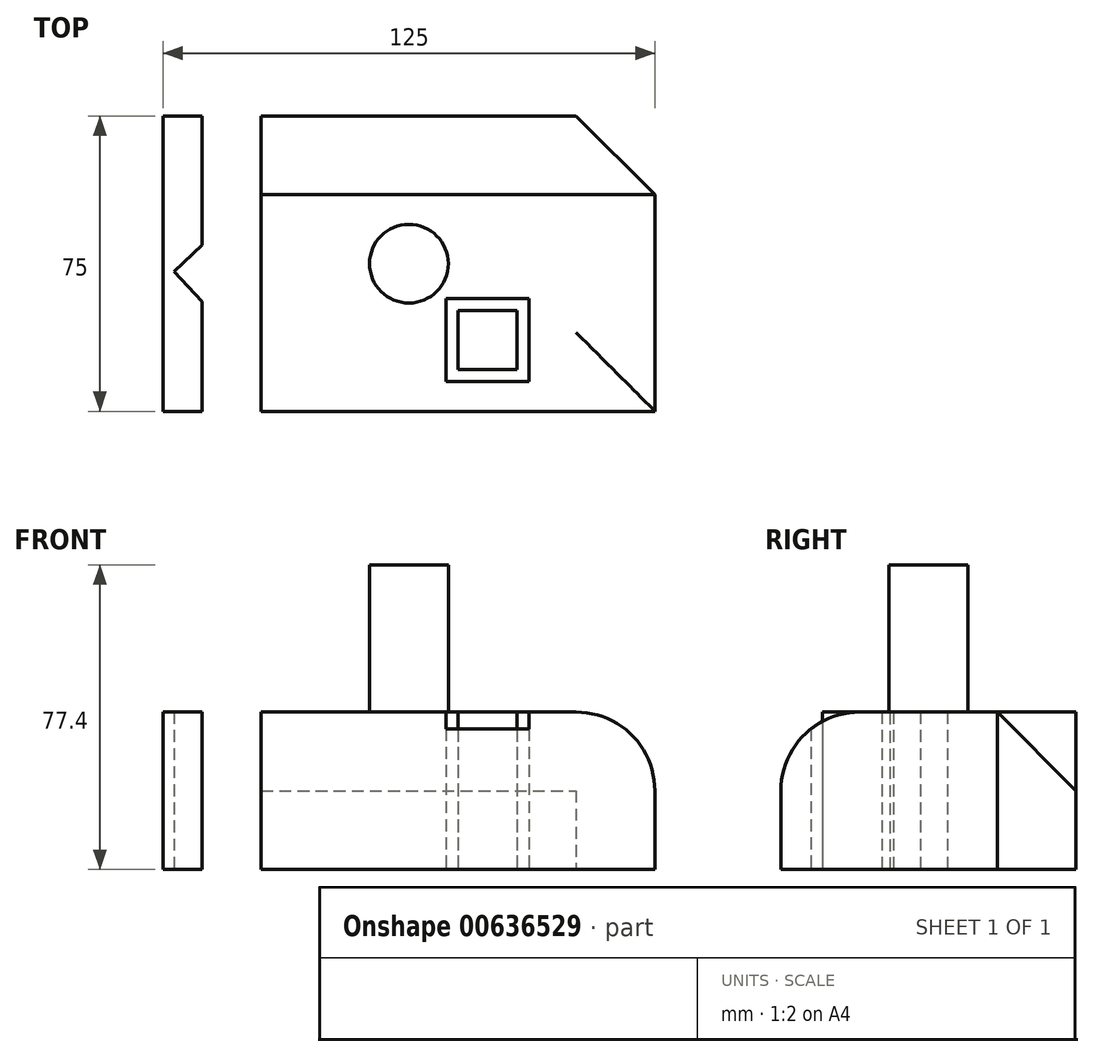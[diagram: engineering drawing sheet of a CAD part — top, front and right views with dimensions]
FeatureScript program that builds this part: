
annotation { "Feature Type Name" : "Feature", "Feature Type Description" : "" }
export const myFeature = defineFeature(function(context is Context, id is Id, definition is map)
    precondition{}
    {
        {
            var Q0;
            Q0=qCreatedBy(makeId("Top.planeOp"),FACE);
            var sketch = newSketch(context, id + "F0", { "sketchPlane" : qUnion([Q0])});
            skLineSegment(sketch, "E0.bottom", {"start": v(62.5, 37.5) * mm, "end": v(-62.5, 37.5) * mm});
            skLineSegment(sketch, "E0.top", {"start": v(62.5, -37.5) * mm, "end": v(-62.5, -37.5) * mm});
            skLineSegment(sketch, "E0.left", {"start": v(62.5, 37.5) * mm, "end": v(62.5, -37.5) * mm});
            skLineSegment(sketch, "E0.right", {"start": v(-62.5, 37.5) * mm, "end": v(-62.5, -37.5) * mm});
            skPoint(sketch, "E0.middle", {"position": v(0, 0) * mm});
            skLineSegment(sketch, "E1.bottom", {"start": v(-52.5, 37.5) * mm, "end": v(-37.5, 37.5) * mm});
            skLineSegment(sketch, "E1.top", {"start": v(-52.5, -37.5) * mm, "end": v(-37.5, -37.5) * mm});
            skLineSegment(sketch, "E1.left", {"start": v(-52.5, 37.5) * mm, "end": v(-52.5, -37.5) * mm});
            skLineSegment(sketch, "E1.right", {"start": v(-37.5, 37.5) * mm, "end": v(-37.5, -37.5) * mm});
            skCircle(sketch, "E2", {"center": v(0, 0) * mm, "radius": 10 * mm});
            skSolve(sketch);
        }
        {
            var Q0;
            {var subQ0=sQuery(id+"F0.wireOp",EDGE,"E0.right");Q0=makeQuery(id+"F0.imprint","IMPRINT",FACE,{"disambiguationData":[TD([[makeQuery(id+"F0.imprint","IMPRINT",EDGE,{"derivedFrom":subQ0}),1.0]])]});}
            var Q1;
            Q1=makeQuery(id+"F0.imprint","IMPRINT",FACE,{"disambiguationData":[TD([[makeQuery(id+"F0.imprint","IMPRINT",EDGE,{"derivedFrom":sQuery(id+"F0.wireOp",EDGE,"E1.bottom")}),-1.0]])]});
            var Q2;
            {var subQ1=sQuery(id+"F0.wireOp",EDGE,"E0.left");Q2=makeQuery(id+"F0.imprint","IMPRINT",FACE,{"disambiguationData":[TD([[makeQuery(id+"F0.imprint","IMPRINT",EDGE,{"derivedFrom":subQ1}),-1.0]])]});}
            var Q3;
            Q3=makeQuery(id+"F0.imprint","IMPRINT",FACE,{"disambiguationData":[TD([[makeQuery(id+"F0.imprint","IMPRINT",EDGE,{"derivedFrom":sQuery(id+"F0.wireOp",EDGE,"E2")}),1.0]])]});
            extrude(context, id + "F1", {"entities" : qUnion([Q0, Q1, Q2, Q3]), "depth" : 40 * mm, "offsetDistance" : 25 * mm});
        }
        {
            var Q0;
            Q0=makeQuery(id+"F1.opExtrude","CAP_FACE",FACE,{"disambiguationData":[OSD([sQuery(id+"F0.wireOp",EDGE,"E0.bottom"),sQuery(id+"F0.wireOp",EDGE,"E0.top"),sQuery(id+"F0.wireOp",EDGE,"E0.left"),sQuery(id+"F0.wireOp",EDGE,"E0.right"),sQuery(id+"F0.wireOp",EDGE,"E1.bottom"),sQuery(id+"F0.wireOp",EDGE,"E1.top")])],"isStart":true});
            var sketch = newSketch(context, id + "F2", { "sketchPlane" : qUnion([Q0])});
            skCircle(sketch, "E3", {"center": v(0, 0) * mm, "radius": 10 * mm});
            skLineSegment(sketch, "E4", {"start": v(-59.7, 2) * mm, "end": v(-43, 19.7) * mm});
            skLineSegment(sketch, "E5", {"start": v(-43, 19.7) * mm, "end": v(-25.3, 3) * mm});
            skLineSegment(sketch, "E6", {"start": v(-25.3, 3) * mm, "end": v(-42, -14.7) * mm});
            skLineSegment(sketch, "E7", {"start": v(-42, -14.7) * mm, "end": v(-59.7, 2) * mm});
            skLineSegment(sketch, "E8", {"start": v(-59.7, 2) * mm, "end": v(-25.3, 3) * mm, "construction": true});
            skLineSegment(sketch, "E9", {"start": v(-43, 19.7) * mm, "end": v(-42, -14.7) * mm, "construction": true});
            skPoint(sketch, "E10", {"position": v(-42.5, 2.5) * mm});
            skArc(sketch, "E11", {"start": v(33.7, -37.5) * mm, "mid": v(50.04, 0.25) * mm, "end": v(32.6, 37.5) * mm});
            skLineSegment(sketch, "E12.bottom", {"start": v(27.45, 11.88) * mm, "end": v(12.45, 11.88) * mm});
            skLineSegment(sketch, "E12.top", {"start": v(27.45, 26.88) * mm, "end": v(12.45, 26.88) * mm});
            skLineSegment(sketch, "E12.left", {"start": v(27.45, 11.88) * mm, "end": v(27.45, 26.88) * mm});
            skLineSegment(sketch, "E12.right", {"start": v(12.45, 11.88) * mm, "end": v(12.45, 26.88) * mm});
            skPoint(sketch, "E12.middle", {"position": v(19.95, 19.38) * mm});
            skLineSegment(sketch, "E13.0", {"start": v(9.45, 8.88) * mm, "end": v(9.45, 29.88) * mm});
            skLineSegment(sketch, "E13.1", {"start": v(30.45, 8.88) * mm, "end": v(9.45, 8.88) * mm});
            skLineSegment(sketch, "E13.2", {"start": v(30.45, 8.88) * mm, "end": v(30.45, 29.88) * mm});
            skLineSegment(sketch, "E13.3", {"start": v(30.45, 29.88) * mm, "end": v(9.45, 29.88) * mm});
            skSolve(sketch);
        }
        {
            var Q0;
            Q0=makeQuery(id+"F2.imprint","IMPRINT",FACE,{"disambiguationData":[TD([[makeQuery(id+"F2.imprint","IMPRINT",EDGE,{"derivedFrom":sQuery(id+"F2.wireOp",EDGE,"E4")}),-1.0]])]});
            var Q1;
            Q1=makeQuery(id+"F2.imprint","IMPRINT",FACE,{"disambiguationData":[TD([[makeQuery(id+"F2.imprint","IMPRINT",EDGE,{"derivedFrom":sQuery(id+"F2.wireOp",EDGE,"E12.bottom")}),1.0]])]});
            extrude(context, id + "F3", {"entities" : qUnion([Q0, Q1]), "operationType" : NewBodyOperationType.REMOVE, "endBound" : BoundingType.THROUGH_ALL, "oppositeDirection" : true, "depth" : 29.7 * mm, "offsetDistance" : 25 * mm});
        }
        {
            var Q0;
            Q0=makeQuery(id+"F2.imprint","IMPRINT",FACE,{"disambiguationData":[TD([[makeQuery(id+"F2.imprint","IMPRINT",EDGE,{"derivedFrom":sQuery(id+"F2.wireOp",EDGE,"E3")}),1.0]])]});
            extrude(context, id + "F4", {"entities" : qUnion([Q0]), "operationType" : NewBodyOperationType.ADD, "oppositeDirection" : true, "depth" : 77.4 * mm, "offsetDistance" : 25 * mm});
        }
        {
            var Q0;
            Q0=makeQuery(id+"F1.opExtrude","CAP_EDGE",EDGE,{"disambiguationData":[OSD([sQuery(id+"F0.wireOp",EDGE,"E0.top"),sQuery(id+"F0.wireOp",EDGE,"E1.top")])],"isStart":false});
            var Q1;
            Q1=makeQuery(id+"F1.opExtrude","CAP_EDGE",EDGE,{"disambiguationData":[OSD([sQuery(id+"F0.wireOp",EDGE,"E0.left")])],"isStart":false});
            fillet(context, id + "F5", {"entities" : qUnion([Q0, Q1]), "radius" : 20 * mm, "tangentPropagation" : true, "allowEdgeOverflow" : false});
        }
        {
            var Q0;
            Q0=makeQuery(id+"F1.opExtrude","CAP_EDGE",EDGE,{"disambiguationData":[OSD([sQuery(id+"F0.wireOp",EDGE,"E0.bottom"),sQuery(id+"F0.wireOp",EDGE,"E1.bottom")])],"isStart":false});
            var Q1;
            Q1=makeQuery(id+"F1.opExtrude","SWEPT_EDGE",EDGE,{"disambiguationData":[OSD([sQuery(id+"F0.wireOp",EDGE,"E0.bottom"),sQuery(id+"F0.wireOp",EDGE,"E0.right")])]});
            chamfer(context, id + "F6", {"entities" : qUnion([Q0, Q1]), "width" : 20 * mm, "tangentPropagation" : true});
        }
    });
